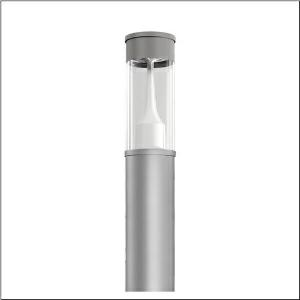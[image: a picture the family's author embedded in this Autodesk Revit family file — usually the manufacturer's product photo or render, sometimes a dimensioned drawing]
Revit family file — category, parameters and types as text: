
# Revit family: city-light_400_iq___st1_2a_5xa5305af14hp_8cfd
name_source: partatom
category: Lighting Fixtures
units: mm (PartAtom-declared; Revit-internal decimal feet)

## family parameters
Cut with Voids When Loaded = No
Host = Face
Light Source = No
Part Type = Normal
Room Calculation Point = No
Round Connector Dimension = Use Diameter
Shared = No

## types (1)
- --- (1 x LED, 3910 lm, 33.6 W, 2200K)
    Apparent Load = 34 VA
    CIE Flux Codes = 22 61 94 96 100
    Color Rendering = 70
    Color Temperature = 2200K
    Default Elevation = 1800 mm
    Description = City-Light 400 iQ, light pillar, Module 540 iQ-SR, primary light control with 3 zone facetted reflector, of plastic, silver coated, highly specular, structured, primary optical cover: cover, of PMMA, transparent, partly coated, light distribution: ST1.2a, primary light characteristic: asymmetric, LED, High Power LED, rated luminous flux: 3.910lm, luminous efficacy: 116lm/W, light colour: 722, colour temperature: 2200K, control gear: ECG iQ, control: presetting dimming logarithmic, Street-Remote, Auto-Match, Temp-Guard, Lumen-Switch, Night-Set, Smart-Wire, Light-Fading, Desk-Remote (wireless, voltage-free reading and setting of iQ features in the workshop via application-optimized NFC function/RFID function), optimised constant luminous flux control (CLO 2.0), with terminal, 6-pole, max. 2.5mm², mains connection: 230..240V, AC, 50/60Hz, start of lifetime: 34W, end of service life: 36W, reduction: 15W, luminaire housing, cylindrical, of extruded aluminium section, coated, Siteco® metallic grey (DB 702S), length: 4.694mm, diameter: 200mm, Module 540 iQ-SR, traffic white (RAL 9016), equipment: Power, protection rating (complete): IP65, insulation class (complete): insulation class II (safety insulation), certification: CE, ENEC, VDE, packaging unit: 1 piece

Light Distribution: ST1.2a
    Height = 500 mm
    Lamp = 1 x LED
    Lamp Light Flux = 3910 lm
    Lamp Power = 33.6 W
    Lamp count = 1
    Length = 200 mm  [stored 0.656168 ft]
    Luminous efficacy = 116 lm/W
    Manufacturer = Siteco
    ModVariant = No
    Model = 5XA5305AF14HP
    Mounting Place = Floor
    Mounting Type = Freestanding
    Number of Poles = 1
    OnlyDefault = Yes
    Power Factor = 1
    Product Name = City-Light 400 iQ | ST1.2a
    Product group = light pillar
    ProductGroupID = 1303
    Protection Class = Protection class II
    Protection Degree = IP 65
    RLX_Detail_Level = 1
    RLX_Emergency_Light_Flux = 0 lm
    RLX_Emergency_Type = 0
    RLX_Emergency_Type_DB = No
    RlxData = <blob elided: 53393 chars, md5=21c4b467>
    Socket = socket
    Standby Power = 0 W
    System Light Flux = 3910 lm
    System Power = 34 W
    Type Comments = factory setting: luminous flux: 100 % | dim-lin: 254 | 695 mA
    Type Image = l_1006916.jpg
    URL = http://relux.com
    VarID = @adj_145543
    Voltage = 0 V
    Weight = 0.00 kg
    Width = 0 mm  [stored 0 ft]

note: [stored X ft] marks values corroborated as IEEE doubles in the binary element streams (Revit-internal decimal feet)

## geometry (parser evidence)
native form markers: Blend x4, Sweep x10
no freeform markers — native parametric forms only
